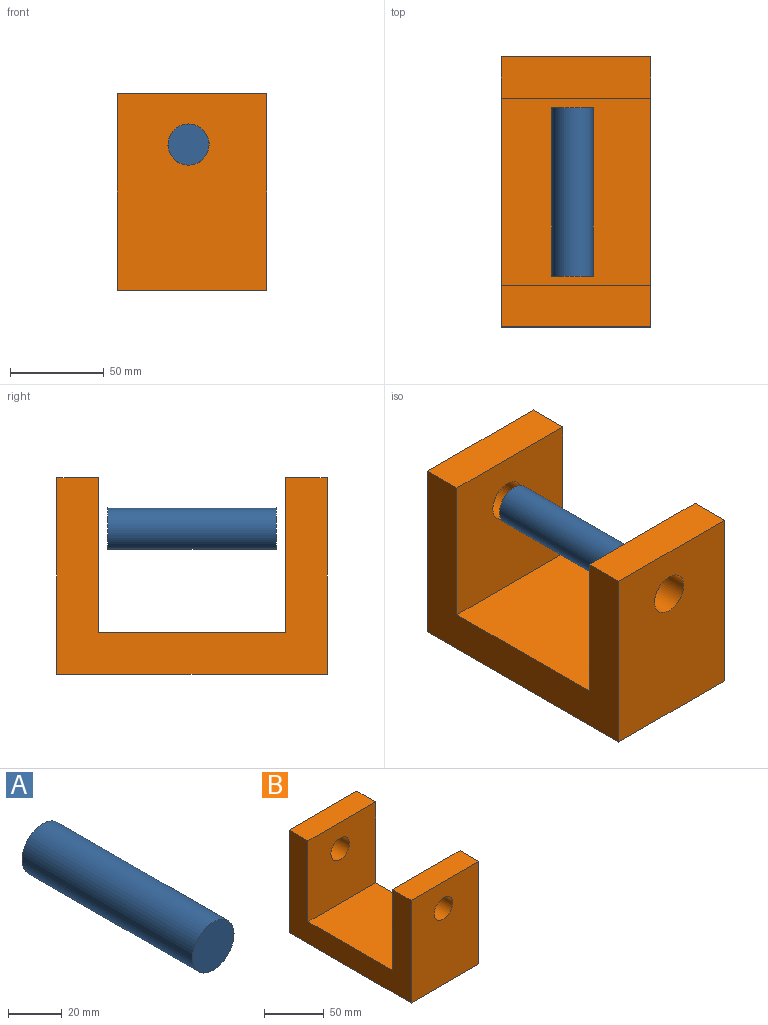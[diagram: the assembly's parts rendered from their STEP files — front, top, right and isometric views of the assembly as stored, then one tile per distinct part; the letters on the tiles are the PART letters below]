
ASSEMBLY  parts=2 mates=1
PART A: 3 faces, bbox 22x90x22 mm
  f0: cylinder r=11mm len=90mm, axis (0,1,0), area 6220.4mm2, adj f1,f2
  f1: plane 22x22mm, normal (0,-1,0), area 380.1mm2, adj f0
  f2: plane 22x22mm, normal (0,1,0), area 380.1mm2, adj f0
PART B: 12 faces, bbox 80x144.4x105.1 mm
  f0: plane 80x22.19mm, normal (0,0,1), area 1775.2mm2, adj f1,f7,f8,f9
  f1: plane 105.11x80mm, normal (0,-1,0), area 8028.6mm2, adj f0,f2,f8,f9,f10
  f2: plane 144.38x80mm, normal (0,0,-1), area 11550.4mm2, adj f1,f3,f8,f9
  f3: plane 105.11x80mm, normal (0,1,0), area 8028.6mm2, adj f2,f4,f8,f9,f11
  f4: plane 80x22.19mm, normal (0,0,1), area 1775.2mm2, adj f3,f5,f8,f9
  f5: plane 82.92x80mm, normal (0,-1,0), area 6253.5mm2, adj f4,f6,f8,f9,f11
  f6: plane 100x80mm, normal (0,0,1), area 8000mm2, adj f5,f7,f8,f9
  f7: plane 82.92x80mm, normal (0,1,0), area 6253.5mm2, adj f0,f6,f8,f9,f10
  f8: plane 144.38x105.11mm, normal (1,0,0), area 6883.7mm2, adj f0,f1,f2,f3,f4,f5,f6,f7
  f9: plane 144.38x105.11mm, normal (-1,0,0), area 6883.7mm2, adj f0,f1,f2,f3,f4,f5,f6,f7
  f10: cylinder r=11mm len=22.19mm, axis (0,1,0), area 1533.6mm2, adj f1,f7
  f11: cylinder r=11mm len=22.19mm, axis (0,1,0), area 1533.6mm2, adj f3,f5
PLACE A t=(-33.4,0.35,-3.45)mm
PLACE B t=(-33.4,0.35,-3.45)mm fixed
MATE fastened A.f0 <-> B.f10  axis (0,1,0) through (4.75,0.35,20.19)mm
